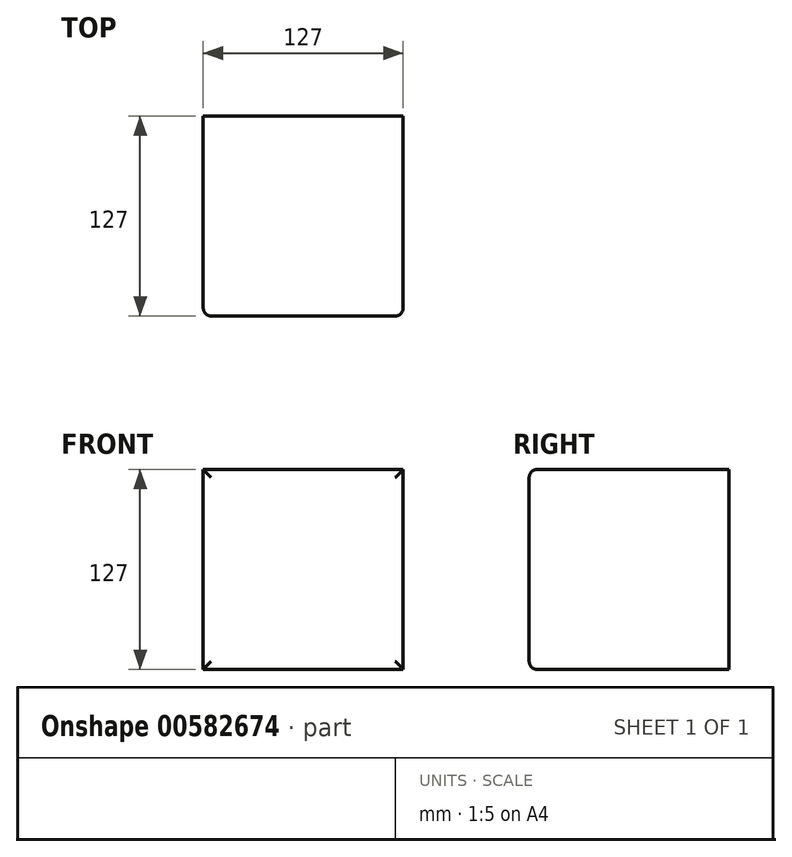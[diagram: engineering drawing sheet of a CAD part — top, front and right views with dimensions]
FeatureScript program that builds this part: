
annotation { "Feature Type Name" : "Feature", "Feature Type Description" : "" }
export const myFeature = defineFeature(function(context is Context, id is Id, definition is map)
    precondition{}
    {
        {
            var Q0;
            Q0=qCreatedBy(makeId("Top.planeOp"),FACE);
            var sketch = newSketch(context, id + "F0", { "sketchPlane" : qUnion([Q0])});
            skLineSegment(sketch, "E0.bottom", {"start": v(63.5, -63.5) * mm, "end": v(-63.5, -63.5) * mm});
            skLineSegment(sketch, "E0.top", {"start": v(63.5, 63.5) * mm, "end": v(-63.5, 63.5) * mm});
            skLineSegment(sketch, "E0.left", {"start": v(63.5, -63.5) * mm, "end": v(63.5, 63.5) * mm});
            skLineSegment(sketch, "E0.right", {"start": v(-63.5, -63.5) * mm, "end": v(-63.5, 63.5) * mm});
            skPoint(sketch, "E0.middle", {"position": v(0, 0) * mm});
            skSolve(sketch);
        }
        {
            var Q0;
            Q0 = qSketchRegion(id + "F0", true);
            extrude(context, id + "F1", {"entities" : qUnion([Q0]), "endBound" : BoundingType.SYMMETRIC, "depth" : 127 * mm, "offsetDistance" : 25.4 * mm});
        }
        {
            var Q0;
            Q0=makeQuery(id+"F1.opExtrude","CAP_EDGE",EDGE,{"disambiguationData":[OSD([sQuery(id+"F0.wireOp",EDGE,"E0.bottom")])],"isStart":false});
            var Q1;
            Q1=makeQuery(id+"F1.opExtrude","SWEPT_EDGE",EDGE,{"disambiguationData":[OSD([sQuery(id+"F0.wireOp",EDGE,"E0.bottom"),sQuery(id+"F0.wireOp",EDGE,"E0.left")])]});
            var Q2;
            Q2=makeQuery(id+"F1.opExtrude","CAP_EDGE",EDGE,{"disambiguationData":[OSD([sQuery(id+"F0.wireOp",EDGE,"E0.bottom")])],"isStart":true});
            var Q3;
            Q3=makeQuery(id+"F1.opExtrude","SWEPT_EDGE",EDGE,{"disambiguationData":[OSD([sQuery(id+"F0.wireOp",EDGE,"E0.bottom"),sQuery(id+"F0.wireOp",EDGE,"E0.right")])]});
            fillet(context, id + "F2", {"entities" : qUnion([Q0, Q1, Q2, Q3]), "radius" : 5.08 * mm, "tangentPropagation" : true, "allowEdgeOverflow" : false});
        }
    });
